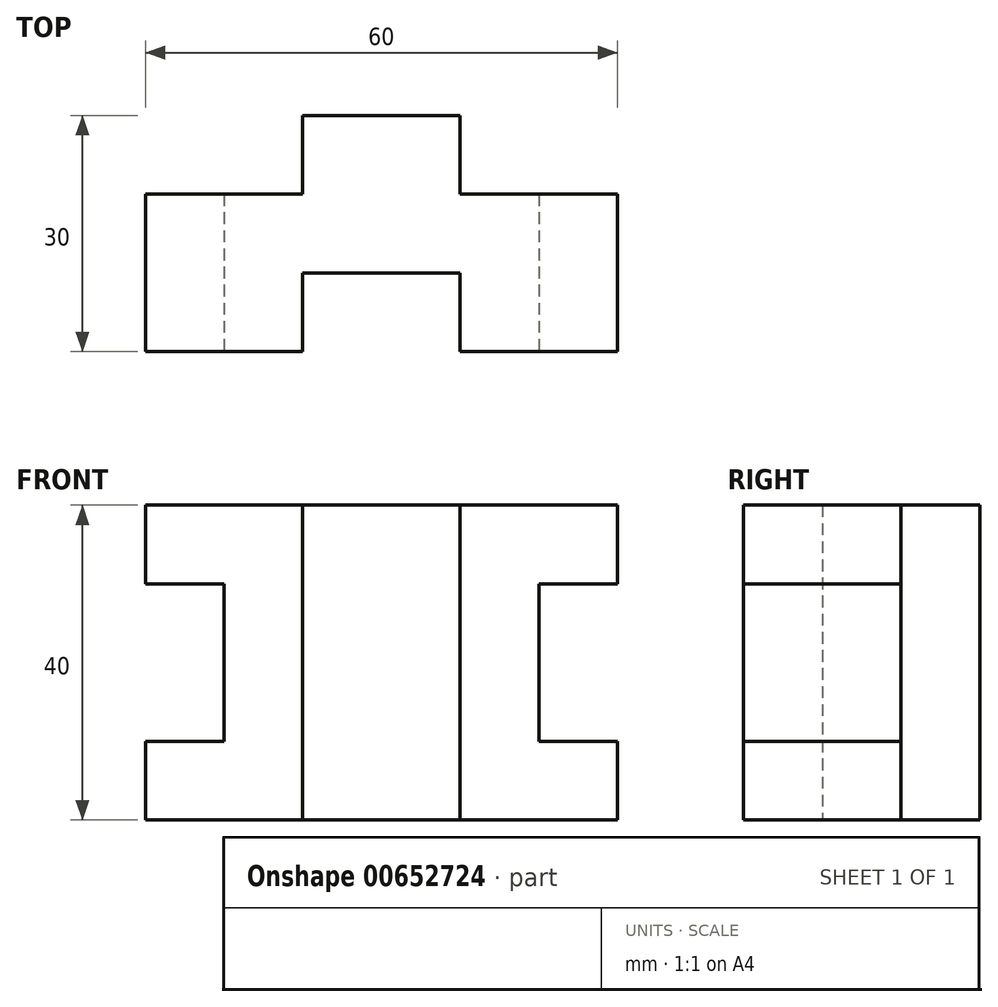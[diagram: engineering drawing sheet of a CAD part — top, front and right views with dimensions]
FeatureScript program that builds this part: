
annotation { "Feature Type Name" : "Feature", "Feature Type Description" : "" }
export const myFeature = defineFeature(function(context is Context, id is Id, definition is map)
    precondition{}
    {
        {
            var Q0;
            Q0=qCreatedBy(makeId("Top.planeOp"),FACE);
            var sketch = newSketch(context, id + "F0", { "sketchPlane" : qUnion([Q0])});
            skLineSegment(sketch, "E0", {"start": v(-53.56, 38.63) * mm, "end": v(-53.56, 18.63) * mm});
            skLineSegment(sketch, "E1", {"start": v(-53.56, 18.63) * mm, "end": v(-33.56, 18.63) * mm});
            skLineSegment(sketch, "E2", {"start": v(-33.56, 18.63) * mm, "end": v(-33.56, 28.63) * mm});
            skLineSegment(sketch, "E3", {"start": v(-33.56, 28.63) * mm, "end": v(-13.56, 28.63) * mm});
            skLineSegment(sketch, "E4", {"start": v(-13.56, 28.63) * mm, "end": v(-13.56, 18.63) * mm});
            skLineSegment(sketch, "E5", {"start": v(-13.56, 18.63) * mm, "end": v(6.44, 18.63) * mm});
            skLineSegment(sketch, "E6", {"start": v(6.44, 18.63) * mm, "end": v(6.44, 38.63) * mm});
            skLineSegment(sketch, "E7", {"start": v(6.44, 38.63) * mm, "end": v(-13.56, 38.63) * mm});
            skLineSegment(sketch, "E8", {"start": v(-13.56, 38.63) * mm, "end": v(-13.56, 48.63) * mm});
            skLineSegment(sketch, "E9", {"start": v(-13.56, 48.63) * mm, "end": v(-33.56, 48.63) * mm});
            skLineSegment(sketch, "E10", {"start": v(-33.56, 48.63) * mm, "end": v(-33.56, 38.63) * mm});
            skLineSegment(sketch, "E11", {"start": v(-33.56, 38.63) * mm, "end": v(-53.56, 38.63) * mm});
            skSolve(sketch);
        }
        {
            var Q0;
            Q0 = qSketchRegion(id + "F0", true);
            extrude(context, id + "F1", {"entities" : qUnion([Q0]), "depth" : 40 * mm, "offsetDistance" : 25 * mm});
        }
        {
            var Q0;
            Q0=makeQuery(id+"F1.opExtrude","SWEPT_FACE",FACE,{"disambiguationData":[OSD([sQuery(id+"F0.wireOp",EDGE,"E1")])]});
            var sketch = newSketch(context, id + "F2", { "sketchPlane" : qUnion([Q0])});
            skLineSegment(sketch, "E12", {"start": v(-53.56, 40) * mm, "end": v(-53.56, 30) * mm});
            skLineSegment(sketch, "E13", {"start": v(-53.56, 30) * mm, "end": v(-43.56, 30) * mm});
            skLineSegment(sketch, "E14", {"start": v(-43.56, 30) * mm, "end": v(-43.56, 10) * mm});
            skLineSegment(sketch, "E15", {"start": v(-43.56, 10) * mm, "end": v(-53.56, 10) * mm});
            skLineSegment(sketch, "E16", {"start": v(-53.56, 10) * mm, "end": v(-53.56, 0) * mm});
            skSolve(sketch);
        }
        {
            var Q0;
            {var subQ0=sQuery(id+"F2.wireOp",EDGE,"E13");Q0=makeQuery(id+"F2.imprint","IMPRINT",FACE,{"disambiguationData":[TD([[makeQuery(id+"F2.imprint","IMPRINT",EDGE,{"derivedFrom":subQ0}),-1.0]])]});}
            extrude(context, id + "F3", {"entities" : qUnion([Q0]), "operationType" : NewBodyOperationType.REMOVE, "endBound" : BoundingType.THROUGH_ALL, "oppositeDirection" : true, "depth" : 25 * mm, "offsetDistance" : 25 * mm});
        }
        {
            var Q0;
            Q0=makeQuery(id+"F1.opExtrude","SWEPT_FACE",FACE,{"disambiguationData":[OSD([sQuery(id+"F0.wireOp",EDGE,"E5")])]});
            var sketch = newSketch(context, id + "F4", { "sketchPlane" : qUnion([Q0])});
            skLineSegment(sketch, "E17", {"start": v(6.44, 40) * mm, "end": v(6.44, 30) * mm});
            skLineSegment(sketch, "E18", {"start": v(6.44, 30) * mm, "end": v(-3.56, 30) * mm});
            skLineSegment(sketch, "E19", {"start": v(-3.56, 30) * mm, "end": v(-3.56, 10) * mm});
            skLineSegment(sketch, "E20", {"start": v(-3.56, 10) * mm, "end": v(6.44, 10) * mm});
            skSolve(sketch);
        }
        {
            var Q0;
            {var subQ0=sQuery(id+"F4.wireOp",EDGE,"E18");Q0=makeQuery(id+"F4.imprint","IMPRINT",FACE,{"disambiguationData":[TD([[makeQuery(id+"F4.imprint","IMPRINT",EDGE,{"derivedFrom":subQ0}),1.0]])]});}
            extrude(context, id + "F5", {"entities" : qUnion([Q0]), "operationType" : NewBodyOperationType.REMOVE, "endBound" : BoundingType.THROUGH_ALL, "oppositeDirection" : true, "depth" : 25 * mm, "offsetDistance" : 25 * mm});
        }
    });
